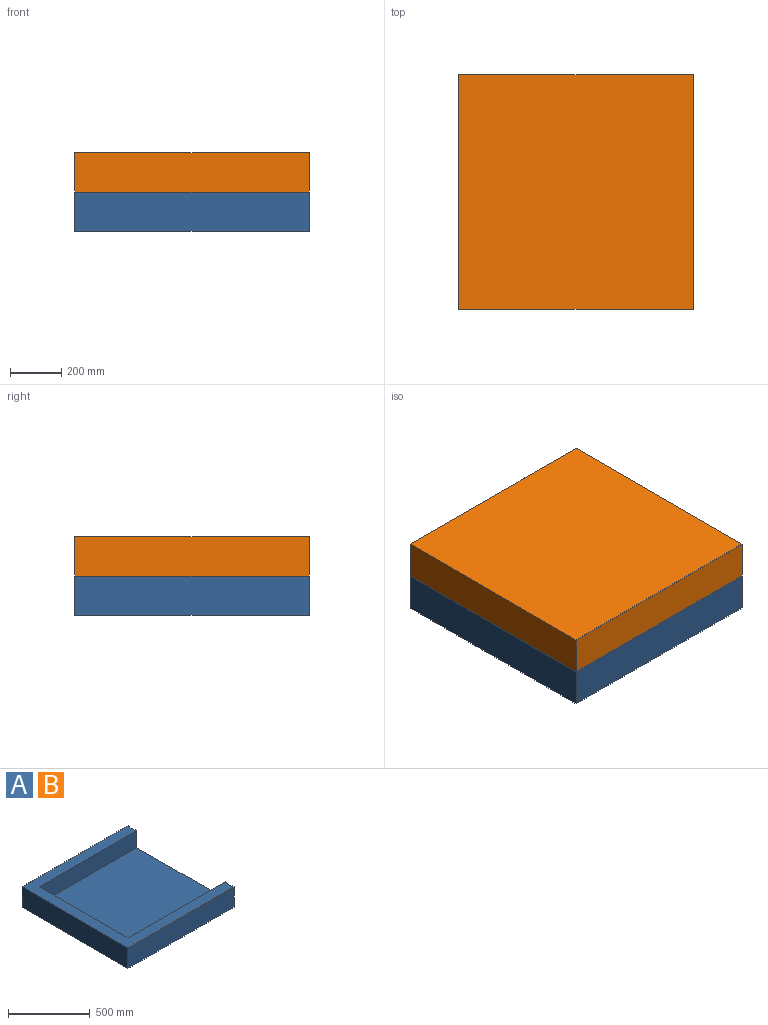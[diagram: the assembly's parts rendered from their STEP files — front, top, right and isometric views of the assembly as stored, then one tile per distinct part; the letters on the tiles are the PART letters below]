
ASSEMBLY  parts=2 mates=1
PART A: 18 faces, bbox 914.4x914.4x152.4 mm
  f0: plane 914.4x152.4mm, normal (1,0,0), area 32258mm2, adj f1,f2,f4,f5,f6,f8,f9,f10
  f1: plane 914.4x914.4mm, normal (0,0,1), area 196773.8mm2, adj f0,f2,f3,f4,f6,f7,f8,f10
  f2: plane 914.4x152.4mm, normal (0,1,0), area 139354.6mm2, adj f0,f1,f3,f5
  f3: plane 914.4x152.4mm, normal (-1,0,0), area 139354.6mm2, adj f1,f2,f4,f5
  f4: plane 914.4x152.4mm, normal (0,-1,0), area 139354.6mm2, adj f0,f1,f3,f5
  f5: plane 914.4x914.4mm, normal (0,0,-1), area 836127.4mm2, adj f0,f2,f3,f4
  f6: plane 838.2x127mm, normal (0,-1,0), area 106451.4mm2, adj f0,f1,f7,f9
  f7: plane 762x127mm, normal (1,0,0), area 96774mm2, adj f1,f6,f8,f9
  f8: plane 838.2x127mm, normal (0,1,0), area 106451.4mm2, adj f0,f1,f7,f9
  f9: plane 838.2x762mm, normal (0,0,1), area 638708.4mm2, adj f0,f6,f7,f8
  f10: plane 101.6x6.35mm, normal (0,1,0), area 645.2mm2, adj f0,f1,f11,f13
  f11: plane 50.8x6.35mm, normal (0,0,1), area 322.6mm2, adj f0,f10,f12,f13
  f12: plane 101.6x6.35mm, normal (0,-1,0), area 645.2mm2, adj f0,f1,f11,f13
  f13: plane 101.6x50.8mm, normal (1,0,0), area 5161.3mm2, adj f1,f10,f11,f12
  f14: plane 101.6x6.35mm, normal (0,1,0), area 645.2mm2, adj f0,f1,f15,f17
  f15: plane 50.8x6.35mm, normal (0,0,1), area 322.6mm2, adj f0,f14,f16,f17
  f16: plane 101.6x6.35mm, normal (0,-1,0), area 645.2mm2, adj f0,f1,f15,f17
  f17: plane 101.6x50.8mm, normal (1,0,0), area 5161.3mm2, adj f1,f14,f15,f16
PART B: same geometry as A
PLACE A t=(-319.36,-107.39,39.29)mm
PLACE B rot(axis=(1,0,0),180deg) t=(-319.36,-107.39,344.09)mm
MATE planar B.f1 <-> A.f1  axis (0,0,-1) through (-444.52,-107.39,191.69)mm
